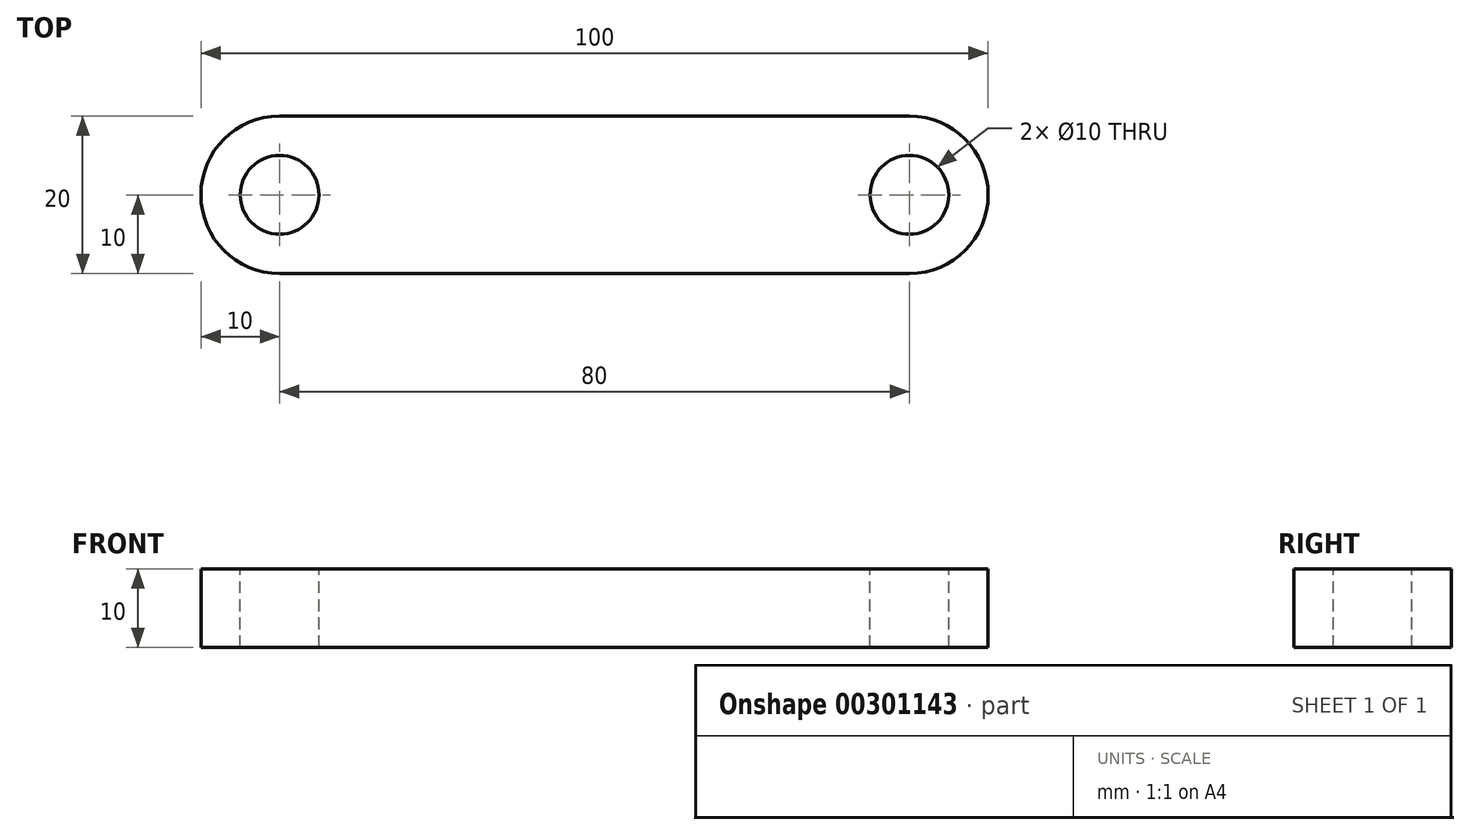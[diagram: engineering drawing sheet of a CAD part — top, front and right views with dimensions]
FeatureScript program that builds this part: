
annotation { "Feature Type Name" : "Feature", "Feature Type Description" : "" }
export const myFeature = defineFeature(function(context is Context, id is Id, definition is map)
    precondition{}
    {
        {
            var Q0;
            Q0=qCreatedBy(makeId("Top.planeOp"),FACE);
            var sketch = newSketch(context, id + "F0", { "sketchPlane" : qUnion([Q0])});
            skLineSegment(sketch, "E0.bottom", {"start": v(0, 0) * mm, "end": v(80, 0) * mm});
            skLineSegment(sketch, "E0.top", {"start": v(0, 20) * mm, "end": v(80, 20) * mm});
            skLineSegment(sketch, "E0.left", {"start": v(0, 0) * mm, "end": v(0, 20) * mm});
            skLineSegment(sketch, "E0.right", {"start": v(80, 0) * mm, "end": v(80, 20) * mm});
            skArc(sketch, "E1", {"start": v(0, 20) * mm, "mid": v(-10, 10) * mm, "end": v(0, 0) * mm});
            skArc(sketch, "E2", {"start": v(80, 0) * mm, "mid": v(90, 10) * mm, "end": v(80, 20) * mm});
            skSolve(sketch);
        }
        {
            var Q0;
            Q0 = qSketchRegion(id + "F0", true);
            extrude(context, id + "F1", {"entities" : qUnion([Q0]), "depth" : 10 * mm});
        }
        {
            var Q0;
            Q0=makeQuery(id+"F1.opExtrude","CAP_FACE",FACE,{"disambiguationData":[OSD([sQuery(id+"F0.wireOp",EDGE,"E0.bottom"),sQuery(id+"F0.wireOp",EDGE,"E0.top"),sQuery(id+"F0.wireOp",EDGE,"E1"),sQuery(id+"F0.wireOp",EDGE,"E2")])],"isStart":false});
            var sketch = newSketch(context, id + "F2", { "sketchPlane" : qUnion([Q0])});
            skCircle(sketch, "E3", {"center": v(0, 10) * mm, "radius": 5 * mm});
            skCircle(sketch, "E4", {"center": v(80, 10) * mm, "radius": 5 * mm});
            skSolve(sketch);
        }
        {
            var Q0;
            Q0 = qSketchRegion(id + "F2", true);
            extrude(context, id + "F3", {"entities" : qUnion([Q0]), "operationType" : NewBodyOperationType.REMOVE, "endBound" : BoundingType.THROUGH_ALL, "oppositeDirection" : true, "depth" : 25 * mm});
        }
    });
